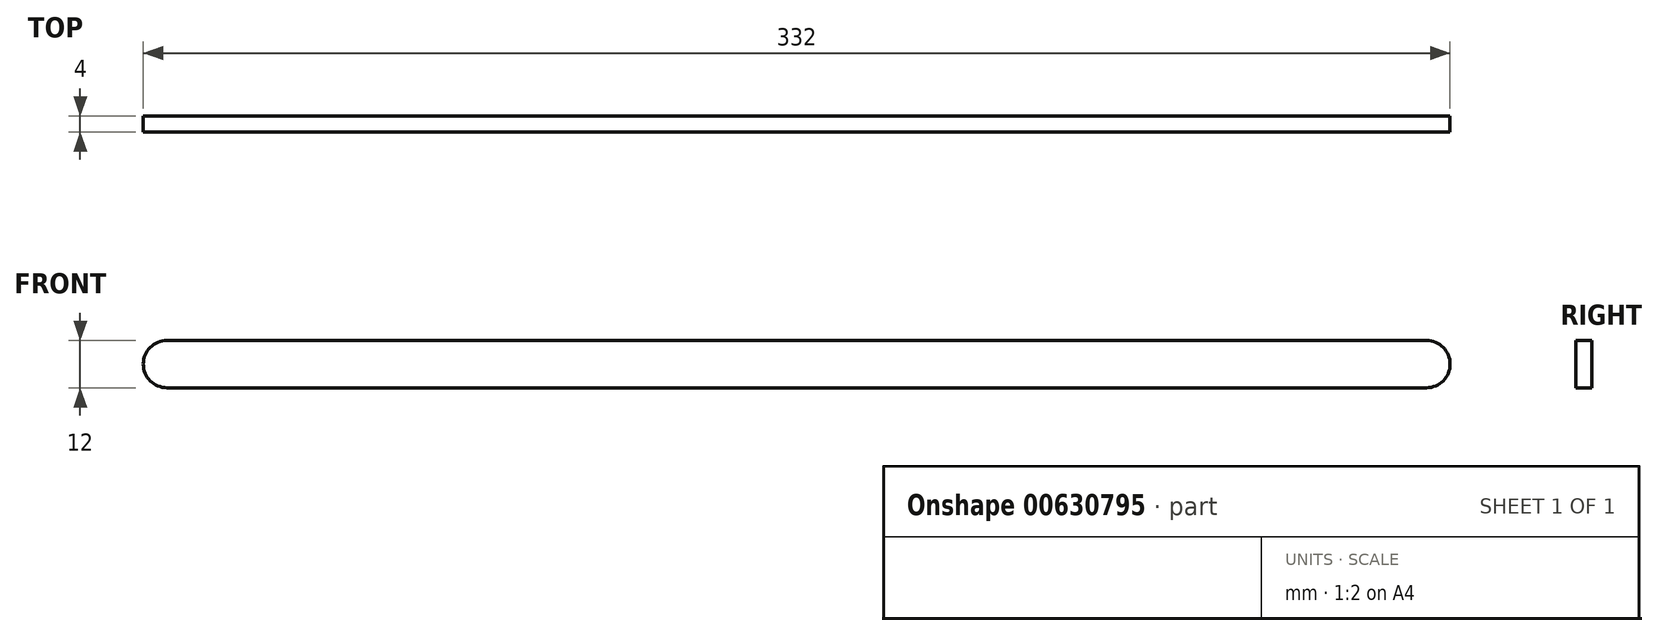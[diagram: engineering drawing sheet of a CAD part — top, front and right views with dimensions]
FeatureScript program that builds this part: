
annotation { "Feature Type Name" : "Feature", "Feature Type Description" : "" }
export const myFeature = defineFeature(function(context is Context, id is Id, definition is map)
    precondition{}
    {
        {
            var Q0;
            Q0=qCreatedBy(makeId("Front.planeOp"),FACE);
            var sketch = newSketch(context, id + "F0", { "sketchPlane" : qUnion([Q0])});
            skLineSegment(sketch, "E0", {"start": v(-28.06, 27.78) * mm, "end": v(291.94, 27.78) * mm});
            skArc(sketch, "E1.0.startCap", {"start": v(-28.06, 21.78) * mm, "mid": v(-34.06, 27.78) * mm, "end": v(-28.06, 33.78) * mm});
            skArc(sketch, "E1.0.endCap", {"start": v(291.94, 33.78) * mm, "mid": v(297.94, 27.78) * mm, "end": v(291.94, 21.78) * mm});
            skLineSegment(sketch, "E1.0.left", {"start": v(-28.06, 33.78) * mm, "end": v(291.94, 33.78) * mm});
            skLineSegment(sketch, "E1.0.right", {"start": v(-28.06, 21.78) * mm, "end": v(291.94, 21.78) * mm});
            skArc(sketch, "E2.0.startCap", {"start": v(-28.06, 20.98) * mm, "mid": v(-34.86, 27.78) * mm, "end": v(-28.06, 34.58) * mm});
            skArc(sketch, "E2.0.endCap", {"start": v(291.94, 34.58) * mm, "mid": v(298.74, 27.78) * mm, "end": v(291.94, 20.98) * mm});
            skLineSegment(sketch, "E2.0.left", {"start": v(-28.06, 34.58) * mm, "end": v(291.94, 34.58) * mm});
            skLineSegment(sketch, "E2.0.right", {"start": v(-28.06, 20.98) * mm, "end": v(291.94, 20.98) * mm});
            skSolve(sketch);
        }
        {
            var Q0;
            Q0=makeQuery(id+"F0.imprint","IMPRINT",FACE,{"disambiguationData":[TD([[makeQuery(id+"F0.imprint","IMPRINT",EDGE,{"derivedFrom":sQuery(id+"F0.wireOp",EDGE,"E1.0.startCap")}),1.0]])]});
            extrude(context, id + "F1", {"entities" : qUnion([Q0]), "depth" : 4 * mm, "offsetDistance" : 25 * mm});
        }
    });
